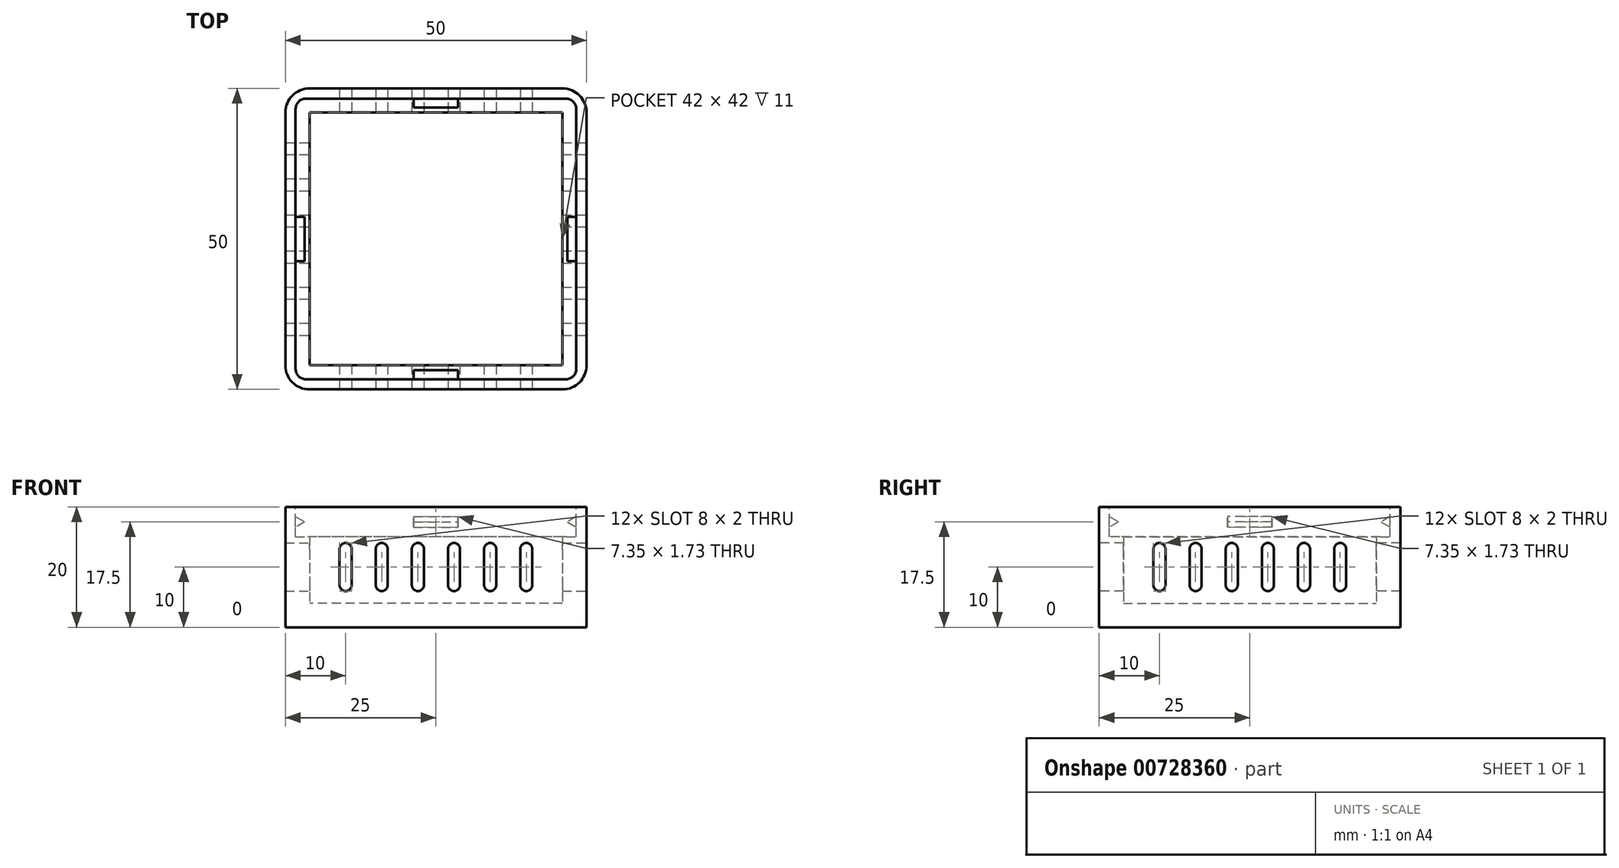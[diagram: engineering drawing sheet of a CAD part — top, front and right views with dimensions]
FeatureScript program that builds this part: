
annotation { "Feature Type Name" : "Feature", "Feature Type Description" : "" }
export const myFeature = defineFeature(function(context is Context, id is Id, definition is map)
    precondition{}
    {
        {
            var Q0;
            Q0=qCreatedBy(makeId("Top.planeOp"),FACE);
            var sketch = newSketch(context, id + "F0", { "sketchPlane" : qUnion([Q0])});
            skLineSegment(sketch, "E0.bottom", {"start": v(25, -25) * mm, "end": v(-25, -25) * mm});
            skLineSegment(sketch, "E0.top", {"start": v(25, 25) * mm, "end": v(-25, 25) * mm});
            skLineSegment(sketch, "E0.left", {"start": v(25, -25) * mm, "end": v(25, 25) * mm});
            skLineSegment(sketch, "E0.right", {"start": v(-25, -25) * mm, "end": v(-25, 25) * mm});
            skPoint(sketch, "E0.middle", {"position": v(0, 0) * mm});
            skSolve(sketch);
        }
        {
            var Q0;
            Q0=qSketchRegion(id+"F0",true);
            extrude(context, id + "F1", {"entities" : qUnion([Q0]), "depth" : 20 * mm, "offsetDistance" : 25 * mm});
        }
        {
            var Q0;
            Q0=makeQuery(id+"F1.opExtrude","CAP_FACE",FACE,{"disambiguationData":[OSD([sQuery(id+"F0.wireOp",EDGE,"E0.bottom"),sQuery(id+"F0.wireOp",EDGE,"E0.top"),sQuery(id+"F0.wireOp",EDGE,"E0.left"),sQuery(id+"F0.wireOp",EDGE,"E0.right")])],"isStart":false});
            shell(context, id + "F2", {"entities" : qUnion([Q0]), "thickness" : 4 * mm});
        }
        {
            var Q0;
            Q0=makeQuery(id+"F1.opExtrude","SWEPT_EDGE",EDGE,{"disambiguationData":[OSD([sQuery(id+"F0.wireOp",EDGE,"E0.bottom"),sQuery(id+"F0.wireOp",EDGE,"E0.right")])]});
            var Q1;
            Q1=makeQuery(id+"F1.opExtrude","SWEPT_EDGE",EDGE,{"disambiguationData":[OSD([sQuery(id+"F0.wireOp",EDGE,"E0.bottom"),sQuery(id+"F0.wireOp",EDGE,"E0.left")])]});
            var Q2;
            Q2=makeQuery(id+"F1.opExtrude","SWEPT_EDGE",EDGE,{"disambiguationData":[OSD([sQuery(id+"F0.wireOp",EDGE,"E0.top"),sQuery(id+"F0.wireOp",EDGE,"E0.left")])]});
            var Q3;
            Q3=makeQuery(id+"F1.opExtrude","SWEPT_EDGE",EDGE,{"disambiguationData":[OSD([sQuery(id+"F0.wireOp",EDGE,"E0.top"),sQuery(id+"F0.wireOp",EDGE,"E0.right")])]});
            fillet(context, id + "F3", {"entities" : qUnion([Q0, Q1, Q2, Q3]), "radius" : 4 * mm, "tangentPropagation" : true, "allowEdgeOverflow" : false});
        }
        {
            var Q0;
            Q0=makeQuery(id+"F1.opExtrude","SWEPT_FACE",FACE,{"disambiguationData":[OSD([sQuery(id+"F0.wireOp",EDGE,"E0.bottom")])]});
            var sketch = newSketch(context, id + "F4", { "sketchPlane" : qUnion([Q0])});
            skLineSegment(sketch, "E1.bottom", {"start": v(-15, 6) * mm, "end": v(-15, 6) * mm});
            skLineSegment(sketch, "E1.top", {"start": v(-15, 14) * mm, "end": v(-15, 14) * mm});
            skLineSegment(sketch, "E1.left", {"start": v(-14, 7) * mm, "end": v(-14, 13) * mm});
            skLineSegment(sketch, "E1.right", {"start": v(-16, 7) * mm, "end": v(-16, 13) * mm});
            skPoint(sketch, "E1.middle", {"position": v(-15, 10) * mm});
            skLineSegment(sketch, "E2.1.0.0", {"start": v(-9, 14) * mm, "end": v(-9, 14) * mm});
            skLineSegment(sketch, "E2.1.0.1", {"start": v(-10, 7) * mm, "end": v(-10, 13) * mm});
            skLineSegment(sketch, "E2.1.0.2", {"start": v(-9, 6) * mm, "end": v(-9, 6) * mm});
            skLineSegment(sketch, "E2.1.0.3", {"start": v(-8, 7) * mm, "end": v(-8, 13) * mm});
            skPoint(sketch, "E2.1.0.4", {"position": v(-9, 10) * mm});
            skLineSegment(sketch, "E2.2.0.0", {"start": v(-3, 14) * mm, "end": v(-3, 14) * mm});
            skLineSegment(sketch, "E2.2.0.1", {"start": v(-4, 7) * mm, "end": v(-4, 13) * mm});
            skLineSegment(sketch, "E2.2.0.2", {"start": v(-3, 6) * mm, "end": v(-3, 6) * mm});
            skLineSegment(sketch, "E2.2.0.3", {"start": v(-2, 7) * mm, "end": v(-2, 13) * mm});
            skPoint(sketch, "E2.2.0.4", {"position": v(-3, 10) * mm});
            skLineSegment(sketch, "E2.3.0.0", {"start": v(3, 14) * mm, "end": v(3, 14) * mm});
            skLineSegment(sketch, "E2.3.0.1", {"start": v(2, 7) * mm, "end": v(2, 13) * mm});
            skLineSegment(sketch, "E2.3.0.2", {"start": v(3, 6) * mm, "end": v(3, 6) * mm});
            skLineSegment(sketch, "E2.3.0.3", {"start": v(4, 7) * mm, "end": v(4, 13) * mm});
            skPoint(sketch, "E2.3.0.4", {"position": v(3, 10) * mm});
            skLineSegment(sketch, "E2.4.0.0", {"start": v(9, 14) * mm, "end": v(9, 14) * mm});
            skLineSegment(sketch, "E2.4.0.1", {"start": v(8, 7) * mm, "end": v(8, 13) * mm});
            skLineSegment(sketch, "E2.4.0.2", {"start": v(9, 6) * mm, "end": v(9, 6) * mm});
            skLineSegment(sketch, "E2.4.0.3", {"start": v(10, 7) * mm, "end": v(10, 13) * mm});
            skPoint(sketch, "E2.4.0.4", {"position": v(9, 10) * mm});
            skLineSegment(sketch, "E2.direction1", {"start": v(-16, 6) * mm, "end": v(-10, 6) * mm, "construction": true});
            skLineSegment(sketch, "E3.MirrorCS", {"start": v(15, 6) * mm, "end": v(15, 6) * mm});
            skLineSegment(sketch, "E4.MirrorCS", {"start": v(16, 7) * mm, "end": v(16, 13) * mm});
            skLineSegment(sketch, "E5.MirrorCS", {"start": v(14, 7) * mm, "end": v(14, 13) * mm});
            skLineSegment(sketch, "E6.MirrorCS", {"start": v(15, 14) * mm, "end": v(15, 14) * mm});
            skPoint(sketch, "E7.MirrorP", {"position": v(15, 10) * mm});
            skLineSegment(sketch, "E8.MirrorCS", {"start": v(16, 6) * mm, "end": v(10, 6) * mm, "construction": true});
            skPoint(sketch, "E9.visualSharp", {"position": v(-16, 14) * mm});
            skArc(sketch, "E9.filletArc", {"start": v(-15, 14) * mm, "mid": v(-15.7, 13.7) * mm, "end": v(-16, 13) * mm});
            skPoint(sketch, "E10.visualSharp", {"position": v(-14, 14) * mm});
            skArc(sketch, "E10.filletArc", {"start": v(-14, 13) * mm, "mid": v(-14.3, 13.7) * mm, "end": v(-15, 14) * mm});
            skPoint(sketch, "E11.visualSharp", {"position": v(-16, 6) * mm});
            skArc(sketch, "E11.filletArc", {"start": v(-16, 7) * mm, "mid": v(-15.7, 6.3) * mm, "end": v(-15, 6) * mm});
            skPoint(sketch, "E12.visualSharp", {"position": v(-14, 6) * mm});
            skArc(sketch, "E12.filletArc", {"start": v(-15, 6) * mm, "mid": v(-14.3, 6.3) * mm, "end": v(-14, 7) * mm});
            skPoint(sketch, "E13.visualSharp", {"position": v(-10, 14) * mm});
            skArc(sketch, "E13.filletArc", {"start": v(-9, 14) * mm, "mid": v(-9.7, 13.7) * mm, "end": v(-10, 13) * mm});
            skPoint(sketch, "E14.visualSharp", {"position": v(-8, 14) * mm});
            skArc(sketch, "E14.filletArc", {"start": v(-8, 13) * mm, "mid": v(-8.3, 13.7) * mm, "end": v(-9, 14) * mm});
            skPoint(sketch, "E15.visualSharp", {"position": v(-8, 6) * mm});
            skArc(sketch, "E15.filletArc", {"start": v(-9, 6) * mm, "mid": v(-8.3, 6.3) * mm, "end": v(-8, 7) * mm});
            skPoint(sketch, "E16.visualSharp", {"position": v(-10, 6) * mm});
            skArc(sketch, "E16.filletArc", {"start": v(-10, 7) * mm, "mid": v(-9.7, 6.3) * mm, "end": v(-9, 6) * mm});
            skPoint(sketch, "E17.visualSharp", {"position": v(-4, 6) * mm});
            skArc(sketch, "E17.filletArc", {"start": v(-4, 7) * mm, "mid": v(-3.7, 6.3) * mm, "end": v(-3, 6) * mm});
            skPoint(sketch, "E18.visualSharp", {"position": v(-2, 6) * mm});
            skArc(sketch, "E18.filletArc", {"start": v(-3, 6) * mm, "mid": v(-2.3, 6.3) * mm, "end": v(-2, 7) * mm});
            skPoint(sketch, "E19.visualSharp", {"position": v(-2, 14) * mm});
            skArc(sketch, "E19.filletArc", {"start": v(-2, 13) * mm, "mid": v(-2.3, 13.7) * mm, "end": v(-3, 14) * mm});
            skPoint(sketch, "E20.visualSharp", {"position": v(-4, 14) * mm});
            skArc(sketch, "E20.filletArc", {"start": v(-3, 14) * mm, "mid": v(-3.7, 13.7) * mm, "end": v(-4, 13) * mm});
            skPoint(sketch, "E21.visualSharp", {"position": v(2, 14) * mm});
            skArc(sketch, "E21.filletArc", {"start": v(3, 14) * mm, "mid": v(2.3, 13.7) * mm, "end": v(2, 13) * mm});
            skPoint(sketch, "E22.visualSharp", {"position": v(4, 14) * mm});
            skArc(sketch, "E22.filletArc", {"start": v(4, 13) * mm, "mid": v(3.7, 13.7) * mm, "end": v(3, 14) * mm});
            skPoint(sketch, "E23.visualSharp", {"position": v(4, 6) * mm});
            skArc(sketch, "E23.filletArc", {"start": v(3, 6) * mm, "mid": v(3.7, 6.3) * mm, "end": v(4, 7) * mm});
            skPoint(sketch, "E24.visualSharp", {"position": v(2, 6) * mm});
            skArc(sketch, "E24.filletArc", {"start": v(2, 7) * mm, "mid": v(2.3, 6.3) * mm, "end": v(3, 6) * mm});
            skPoint(sketch, "E25.visualSharp", {"position": v(10, 14) * mm});
            skArc(sketch, "E25.filletArc", {"start": v(10, 13) * mm, "mid": v(9.7, 13.7) * mm, "end": v(9, 14) * mm});
            skPoint(sketch, "E26.visualSharp", {"position": v(8, 14) * mm});
            skArc(sketch, "E26.filletArc", {"start": v(9, 14) * mm, "mid": v(8.3, 13.7) * mm, "end": v(8, 13) * mm});
            skPoint(sketch, "E27.visualSharp", {"position": v(8, 6) * mm});
            skArc(sketch, "E27.filletArc", {"start": v(8, 7) * mm, "mid": v(8.3, 6.3) * mm, "end": v(9, 6) * mm});
            skPoint(sketch, "E28.visualSharp", {"position": v(10, 6) * mm});
            skArc(sketch, "E28.filletArc", {"start": v(9, 6) * mm, "mid": v(9.7, 6.3) * mm, "end": v(10, 7) * mm});
            skPoint(sketch, "E29.visualSharp", {"position": v(16, 14) * mm});
            skArc(sketch, "E29.filletArc", {"start": v(16, 13) * mm, "mid": v(15.7, 13.7) * mm, "end": v(15, 14) * mm});
            skPoint(sketch, "E30.visualSharp", {"position": v(14, 14) * mm});
            skArc(sketch, "E30.filletArc", {"start": v(15, 14) * mm, "mid": v(14.3, 13.7) * mm, "end": v(14, 13) * mm});
            skPoint(sketch, "E31.visualSharp", {"position": v(16, 6) * mm});
            skArc(sketch, "E31.filletArc", {"start": v(15, 6) * mm, "mid": v(15.7, 6.3) * mm, "end": v(16, 7) * mm});
            skPoint(sketch, "E32.visualSharp", {"position": v(14, 6) * mm});
            skArc(sketch, "E32.filletArc", {"start": v(14, 7) * mm, "mid": v(14.3, 6.3) * mm, "end": v(15, 6) * mm});
            skSolve(sketch);
        }
        {
            var Q0;
            Q0=qSketchRegion(id+"F4",true);
            extrude(context, id + "F5", {"entities" : qUnion([Q0]), "operationType" : NewBodyOperationType.REMOVE, "oppositeDirection" : true, "depth" : 50 * mm, "offsetDistance" : 25 * mm});
        }
        {
            var Q0;
            Q0=makeQuery(id+"F1.opExtrude","SWEPT_FACE",FACE,{"disambiguationData":[OSD([sQuery(id+"F0.wireOp",EDGE,"E0.left")])]});
            var sketch = newSketch(context, id + "F6", { "sketchPlane" : qUnion([Q0])});
            skLineSegment(sketch, "E33.bottom", {"start": v(-15, 6) * mm, "end": v(-15, 6) * mm});
            skLineSegment(sketch, "E33.top", {"start": v(-15, 14) * mm, "end": v(-15, 14) * mm});
            skLineSegment(sketch, "E33.left", {"start": v(-14, 7) * mm, "end": v(-14, 13) * mm});
            skLineSegment(sketch, "E33.right", {"start": v(-16, 7) * mm, "end": v(-16, 13) * mm});
            skPoint(sketch, "E33.middle", {"position": v(-15, 10) * mm});
            skPoint(sketch, "E34.visualSharp", {"position": v(-16, 14) * mm});
            skArc(sketch, "E34.filletArc", {"start": v(-15, 14) * mm, "mid": v(-15.7, 13.7) * mm, "end": v(-16, 13) * mm});
            skPoint(sketch, "E35.visualSharp", {"position": v(-14, 14) * mm});
            skArc(sketch, "E35.filletArc", {"start": v(-14, 13) * mm, "mid": v(-14.3, 13.7) * mm, "end": v(-15, 14) * mm});
            skPoint(sketch, "E36.visualSharp", {"position": v(-14, 6) * mm});
            skArc(sketch, "E36.filletArc", {"start": v(-15, 6) * mm, "mid": v(-14.3, 6.3) * mm, "end": v(-14, 7) * mm});
            skPoint(sketch, "E37.visualSharp", {"position": v(-16, 6) * mm});
            skArc(sketch, "E37.filletArc", {"start": v(-16, 7) * mm, "mid": v(-15.7, 6.3) * mm, "end": v(-15, 6) * mm});
            skPoint(sketch, "E38.1.0.0", {"position": v(-8, 6) * mm});
            skPoint(sketch, "E38.1.0.1", {"position": v(-10, 6) * mm});
            skLineSegment(sketch, "E38.1.0.2", {"start": v(-10, 7) * mm, "end": v(-10, 13) * mm});
            skLineSegment(sketch, "E38.1.0.3", {"start": v(-8, 7) * mm, "end": v(-8, 13) * mm});
            skPoint(sketch, "E38.1.0.4", {"position": v(-8, 14) * mm});
            skPoint(sketch, "E38.1.0.5", {"position": v(-10, 14) * mm});
            skPoint(sketch, "E38.1.0.6", {"position": v(-9, 10) * mm});
            skArc(sketch, "E38.1.0.7", {"start": v(-9, 6) * mm, "mid": v(-8.3, 6.3) * mm, "end": v(-8, 7) * mm});
            skArc(sketch, "E38.1.0.8", {"start": v(-8, 13) * mm, "mid": v(-8.3, 13.7) * mm, "end": v(-9, 14) * mm});
            skArc(sketch, "E38.1.0.9", {"start": v(-9, 14) * mm, "mid": v(-9.7, 13.7) * mm, "end": v(-10, 13) * mm});
            skArc(sketch, "E38.1.0.10", {"start": v(-10, 7) * mm, "mid": v(-9.7, 6.3) * mm, "end": v(-9, 6) * mm});
            skPoint(sketch, "E38.2.0.0", {"position": v(-2, 6) * mm});
            skPoint(sketch, "E38.2.0.1", {"position": v(-4, 6) * mm});
            skLineSegment(sketch, "E38.2.0.2", {"start": v(-4, 7) * mm, "end": v(-4, 13) * mm});
            skLineSegment(sketch, "E38.2.0.3", {"start": v(-2, 7) * mm, "end": v(-2, 13) * mm});
            skPoint(sketch, "E38.2.0.4", {"position": v(-2, 14) * mm});
            skPoint(sketch, "E38.2.0.5", {"position": v(-4, 14) * mm});
            skPoint(sketch, "E38.2.0.6", {"position": v(-3, 10) * mm});
            skArc(sketch, "E38.2.0.7", {"start": v(-3, 6) * mm, "mid": v(-2.3, 6.3) * mm, "end": v(-2, 7) * mm});
            skArc(sketch, "E38.2.0.8", {"start": v(-2, 13) * mm, "mid": v(-2.3, 13.7) * mm, "end": v(-3, 14) * mm});
            skArc(sketch, "E38.2.0.9", {"start": v(-3, 14) * mm, "mid": v(-3.7, 13.7) * mm, "end": v(-4, 13) * mm});
            skArc(sketch, "E38.2.0.10", {"start": v(-4, 7) * mm, "mid": v(-3.7, 6.3) * mm, "end": v(-3, 6) * mm});
            skLineSegment(sketch, "E38.direction1", {"start": v(-16, 6) * mm, "end": v(-10, 6) * mm, "construction": true});
            skArc(sketch, "E39.MirrorCS", {"start": v(10, 7) * mm, "mid": v(9.7, 6.3) * mm, "end": v(9, 6) * mm});
            skArc(sketch, "E40.MirrorCS", {"start": v(9, 14) * mm, "mid": v(9.7, 13.7) * mm, "end": v(10, 13) * mm});
            skArc(sketch, "E41.MirrorCS", {"start": v(9, 6) * mm, "mid": v(8.3, 6.3) * mm, "end": v(8, 7) * mm});
            skArc(sketch, "E42.MirrorCS", {"start": v(16, 7) * mm, "mid": v(15.7, 6.3) * mm, "end": v(15, 6) * mm});
            skArc(sketch, "E43.MirrorCS", {"start": v(15, 6) * mm, "mid": v(14.3, 6.3) * mm, "end": v(14, 7) * mm});
            skArc(sketch, "E44.MirrorCS", {"start": v(14, 13) * mm, "mid": v(14.3, 13.7) * mm, "end": v(15, 14) * mm});
            skArc(sketch, "E45.MirrorCS", {"start": v(2, 13) * mm, "mid": v(2.3, 13.7) * mm, "end": v(3, 14) * mm});
            skArc(sketch, "E46.MirrorCS", {"start": v(3, 6) * mm, "mid": v(2.3, 6.3) * mm, "end": v(2, 7) * mm});
            skArc(sketch, "E47.MirrorCS", {"start": v(4, 7) * mm, "mid": v(3.7, 6.3) * mm, "end": v(3, 6) * mm});
            skArc(sketch, "E48.MirrorCS", {"start": v(8, 13) * mm, "mid": v(8.3, 13.7) * mm, "end": v(9, 14) * mm});
            skArc(sketch, "E49.MirrorCS", {"start": v(15, 14) * mm, "mid": v(15.7, 13.7) * mm, "end": v(16, 13) * mm});
            skArc(sketch, "E50.MirrorCS", {"start": v(3, 14) * mm, "mid": v(3.7, 13.7) * mm, "end": v(4, 13) * mm});
            skPoint(sketch, "E51.MirrorP", {"position": v(9, 10) * mm});
            skLineSegment(sketch, "E52.MirrorCS", {"start": v(4, 7) * mm, "end": v(4, 13) * mm});
            skLineSegment(sketch, "E53.MirrorCS", {"start": v(16, 6) * mm, "end": v(10, 6) * mm, "construction": true});
            skPoint(sketch, "E54.MirrorP", {"position": v(14, 14) * mm});
            skLineSegment(sketch, "E55.MirrorCS", {"start": v(8, 7) * mm, "end": v(8, 13) * mm});
            skPoint(sketch, "E56.MirrorP", {"position": v(4, 6) * mm});
            skPoint(sketch, "E57.MirrorP", {"position": v(14, 6) * mm});
            skPoint(sketch, "E58.MirrorP", {"position": v(4, 14) * mm});
            skLineSegment(sketch, "E59.MirrorCS", {"start": v(10, 7) * mm, "end": v(10, 13) * mm});
            skPoint(sketch, "E60.MirrorP", {"position": v(10, 6) * mm});
            skLineSegment(sketch, "E61.MirrorCS", {"start": v(15, 14) * mm, "end": v(15, 14) * mm});
            skLineSegment(sketch, "E62.MirrorCS", {"start": v(16, 7) * mm, "end": v(16, 13) * mm});
            skLineSegment(sketch, "E63.MirrorCS", {"start": v(14, 7) * mm, "end": v(14, 13) * mm});
            skLineSegment(sketch, "E64.MirrorCS", {"start": v(2, 7) * mm, "end": v(2, 13) * mm});
            skPoint(sketch, "E65.MirrorP", {"position": v(16, 14) * mm});
            skPoint(sketch, "E66.MirrorP", {"position": v(8, 14) * mm});
            skPoint(sketch, "E67.MirrorP", {"position": v(16, 6) * mm});
            skPoint(sketch, "E68.MirrorP", {"position": v(2, 14) * mm});
            skPoint(sketch, "E69.MirrorP", {"position": v(2, 6) * mm});
            skPoint(sketch, "E70.MirrorP", {"position": v(3, 10) * mm});
            skLineSegment(sketch, "E71.MirrorCS", {"start": v(15, 6) * mm, "end": v(15, 6) * mm});
            skPoint(sketch, "E72.MirrorP", {"position": v(15, 10) * mm});
            skPoint(sketch, "E73.MirrorP", {"position": v(8, 6) * mm});
            skPoint(sketch, "E74.MirrorP", {"position": v(10, 14) * mm});
            skSolve(sketch);
        }
        {
            var Q0;
            Q0=qSketchRegion(id+"F6",true);
            extrude(context, id + "F7", {"entities" : qUnion([Q0]), "operationType" : NewBodyOperationType.REMOVE, "endBound" : BoundingType.THROUGH_ALL, "oppositeDirection" : true, "depth" : 25 * mm, "offsetDistance" : 25 * mm});
        }
        {
            var Q0;
            Q0=makeQuery(id+"F1.opExtrude","CAP_FACE",FACE,{"disambiguationData":[OSD([sQuery(id+"F0.wireOp",EDGE,"E0.bottom"),sQuery(id+"F0.wireOp",EDGE,"E0.top"),sQuery(id+"F0.wireOp",EDGE,"E0.left"),sQuery(id+"F0.wireOp",EDGE,"E0.right")])],"isStart":false});
            var sketch = newSketch(context, id + "F8", { "sketchPlane" : qUnion([Q0])});
            skLineSegment(sketch, "E75.bottom", {"start": v(23.3, 23.3) * mm, "end": v(-23.3, 23.3) * mm});
            skLineSegment(sketch, "E75.top", {"start": v(23.3, -23.3) * mm, "end": v(-23.3, -23.3) * mm});
            skLineSegment(sketch, "E75.left", {"start": v(23.3, 23.3) * mm, "end": v(23.3, -23.3) * mm});
            skLineSegment(sketch, "E75.right", {"start": v(-23.3, 23.3) * mm, "end": v(-23.3, -23.3) * mm});
            skPoint(sketch, "E75.middle", {"position": v(0, 0) * mm});
            skSolve(sketch);
        }
        {
            var Q0;
            Q0=qSketchRegion(id+"F8",true);
            extrude(context, id + "F9", {"entities" : qUnion([Q0]), "operationType" : NewBodyOperationType.REMOVE, "oppositeDirection" : true, "depth" : 5 * mm, "offsetDistance" : 25 * mm});
        }
        {
            var Q0;
            Q0=makeQuery(id+"F9.boolean.opBoolean","COPY",EDGE,{"derivedFrom":makeQuery(id+"F9.opExtrude","SWEPT_EDGE",EDGE,{"disambiguationData":[OSD([sQuery(id+"F8.wireOp",EDGE,"E75.bottom"),sQuery(id+"F8.wireOp",EDGE,"E75.right")])]})});
            var Q1;
            Q1=makeQuery(id+"F9.boolean.opBoolean","COPY",EDGE,{"derivedFrom":makeQuery(id+"F9.opExtrude","SWEPT_EDGE",EDGE,{"disambiguationData":[OSD([sQuery(id+"F8.wireOp",EDGE,"E75.bottom"),sQuery(id+"F8.wireOp",EDGE,"E75.left")])]})});
            var Q2;
            Q2=makeQuery(id+"F9.boolean.opBoolean","COPY",EDGE,{"derivedFrom":makeQuery(id+"F9.opExtrude","SWEPT_EDGE",EDGE,{"disambiguationData":[OSD([sQuery(id+"F8.wireOp",EDGE,"E75.top"),sQuery(id+"F8.wireOp",EDGE,"E75.left")])]})});
            var Q3;
            Q3=makeQuery(id+"F9.boolean.opBoolean","COPY",EDGE,{"derivedFrom":makeQuery(id+"F9.opExtrude","SWEPT_EDGE",EDGE,{"disambiguationData":[OSD([sQuery(id+"F8.wireOp",EDGE,"E75.top"),sQuery(id+"F8.wireOp",EDGE,"E75.right")])]})});
            fillet(context, id + "F10", {"entities" : qUnion([Q0, Q1, Q2, Q3]), "radius" : 1.7 * mm, "tangentPropagation" : true, "allowEdgeOverflow" : false});
        }
        {
            var Q0;
            Q0=qCreatedBy(makeId("Right.planeOp"),FACE);
            var sketch = newSketch(context, id + "F11", { "sketchPlane" : qUnion([Q0])});
            skLineSegment(sketch, "E76", {"start": v(23.3, 18.37) * mm, "end": v(21.8, 17.5) * mm});
            skLineSegment(sketch, "E77", {"start": v(21.8, 17.5) * mm, "end": v(23.3, 16.63) * mm});
            skLineSegment(sketch, "E78", {"start": v(23.3, 16.63) * mm, "end": v(23.3, 18.37) * mm});
            skLineSegment(sketch, "E79.MirrorCS", {"start": v(-23.3, 18.37) * mm, "end": v(-21.8, 17.5) * mm});
            skLineSegment(sketch, "E80.MirrorCS", {"start": v(-21.8, 17.5) * mm, "end": v(-23.3, 16.63) * mm});
            skLineSegment(sketch, "E81.MirrorCS", {"start": v(-23.3, 16.63) * mm, "end": v(-23.3, 18.37) * mm});
            skSolve(sketch);
        }
        {
            var Q0;
            Q0=qSketchRegion(id+"F11",true);
            extrude(context, id + "F12", {"entities" : qUnion([Q0]), "operationType" : NewBodyOperationType.ADD, "endBound" : BoundingType.SYMMETRIC, "oppositeDirection" : true, "depth" : 7.35 * mm, "offsetDistance" : 25 * mm});
        }
        {
            var Q0;
            Q0=qCreatedBy(makeId("Front.planeOp"),FACE);
            var sketch = newSketch(context, id + "F13", { "sketchPlane" : qUnion([Q0])});
            skLineSegment(sketch, "E82", {"start": v(23.3, 18.37) * mm, "end": v(21.8, 17.5) * mm});
            skLineSegment(sketch, "E83", {"start": v(21.8, 17.5) * mm, "end": v(23.3, 16.63) * mm});
            skLineSegment(sketch, "E84", {"start": v(23.3, 16.63) * mm, "end": v(23.3, 18.37) * mm});
            skLineSegment(sketch, "E85.MirrorCS", {"start": v(-23.3, 18.37) * mm, "end": v(-21.8, 17.5) * mm});
            skLineSegment(sketch, "E86.MirrorCS", {"start": v(-21.8, 17.5) * mm, "end": v(-23.3, 16.63) * mm});
            skLineSegment(sketch, "E87.MirrorCS", {"start": v(-23.3, 16.63) * mm, "end": v(-23.3, 18.37) * mm});
            skSolve(sketch);
        }
        {
            var Q0;
            Q0=qSketchRegion(id+"F13",true);
            extrude(context, id + "F14", {"entities" : qUnion([Q0]), "operationType" : NewBodyOperationType.ADD, "endBound" : BoundingType.SYMMETRIC, "oppositeDirection" : true, "depth" : 7.35 * mm, "offsetDistance" : 25 * mm});
        }
    });
